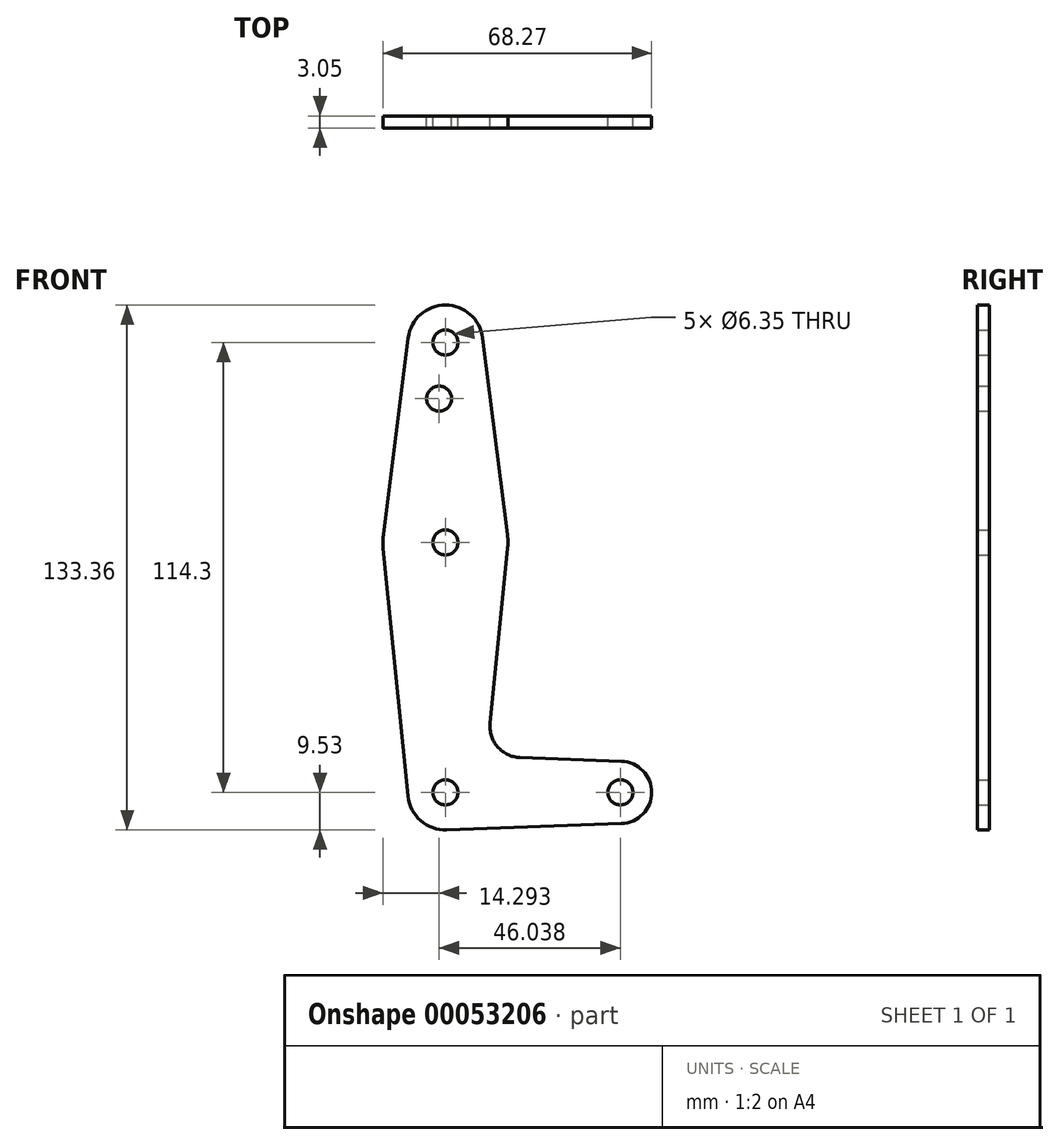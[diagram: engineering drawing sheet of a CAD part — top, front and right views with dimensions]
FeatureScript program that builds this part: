
annotation { "Feature Type Name" : "Feature", "Feature Type Description" : "" }
export const myFeature = defineFeature(function(context is Context, id is Id, definition is map)
    precondition{}
    {
        {
            var Q0;
            Q0=qCreatedBy(makeId("Front.planeOp"),FACE);
            var sketch = newSketch(context, id + "F0", { "sketchPlane" : qUnion([Q0])});
            skLineSegment(sketch, "E0", {"start": v(0, 0) * mm, "end": v(0, 114.3) * mm, "construction": true});
            skLineSegment(sketch, "E1", {"start": v(0, 0) * mm, "end": v(44.45, 0) * mm, "construction": true});
            skArc(sketch, "E2", {"start": v(9.45, 115.5) * mm, "mid": v(0, 123.83) * mm, "end": v(-9.45, 115.5) * mm});
            skArc(sketch, "E3", {"start": v(-9.48, -0.95) * mm, "mid": v(-6.26, -7.18) * mm, "end": v(0.34, -9.52) * mm});
            skArc(sketch, "E4", {"start": v(44.73, -7.93) * mm, "mid": v(52.39, 0) * mm, "end": v(44.73, 7.93) * mm});
            skArc(sketch, "E5", {"start": v(-15.75, 65.48) * mm, "mid": v(-15.87, 63.7) * mm, "end": v(-15.8, 61.91) * mm});
            skLineSegment(sketch, "E6", {"start": v(-9.45, 115.5) * mm, "end": v(-15.75, 65.48) * mm});
            skLineSegment(sketch, "E7", {"start": v(9.45, 115.5) * mm, "end": v(15.75, 65.48) * mm});
            skLineSegment(sketch, "E8", {"start": v(15.8, 61.91) * mm, "end": v(11.34, 17.6) * mm});
            skLineSegment(sketch, "E9", {"start": v(18.97, 8.85) * mm, "end": v(44.73, 7.93) * mm});
            skLineSegment(sketch, "E10", {"start": v(0.34, -9.52) * mm, "end": v(44.73, -7.93) * mm});
            skCircle(sketch, "E11", {"center": v(-1.59, 100.03) * mm, "radius": 3.18 * mm});
            skCircle(sketch, "E12", {"center": v(0, 63.5) * mm, "radius": 3.18 * mm});
            skCircle(sketch, "E13", {"center": v(0, 0) * mm, "radius": 3.18 * mm});
            skCircle(sketch, "E14", {"center": v(44.45, 0) * mm, "radius": 3.18 * mm});
            skCircle(sketch, "E15", {"center": v(0, 114.3) * mm, "radius": 3.18 * mm});
            skArc(sketch, "E16.filletArc", {"start": v(11.34, 17.6) * mm, "mid": v(13.26, 11.57) * mm, "end": v(18.97, 8.85) * mm});
            skArc(sketch, "E17.trimOffspring", {"start": v(15.8, 61.91) * mm, "mid": v(15.87, 63.7) * mm, "end": v(15.75, 65.48) * mm});
            skLineSegment(sketch, "E18", {"start": v(-15.8, 61.91) * mm, "end": v(-9.48, -0.95) * mm});
            skSolve(sketch);
        }
        {
            var Q0;
            Q0 = qSketchRegion(id + "F0", true);
            extrude(context, id + "F1", {"entities" : qUnion([Q0]), "depth" : 3.05 * mm});
        }
    });
